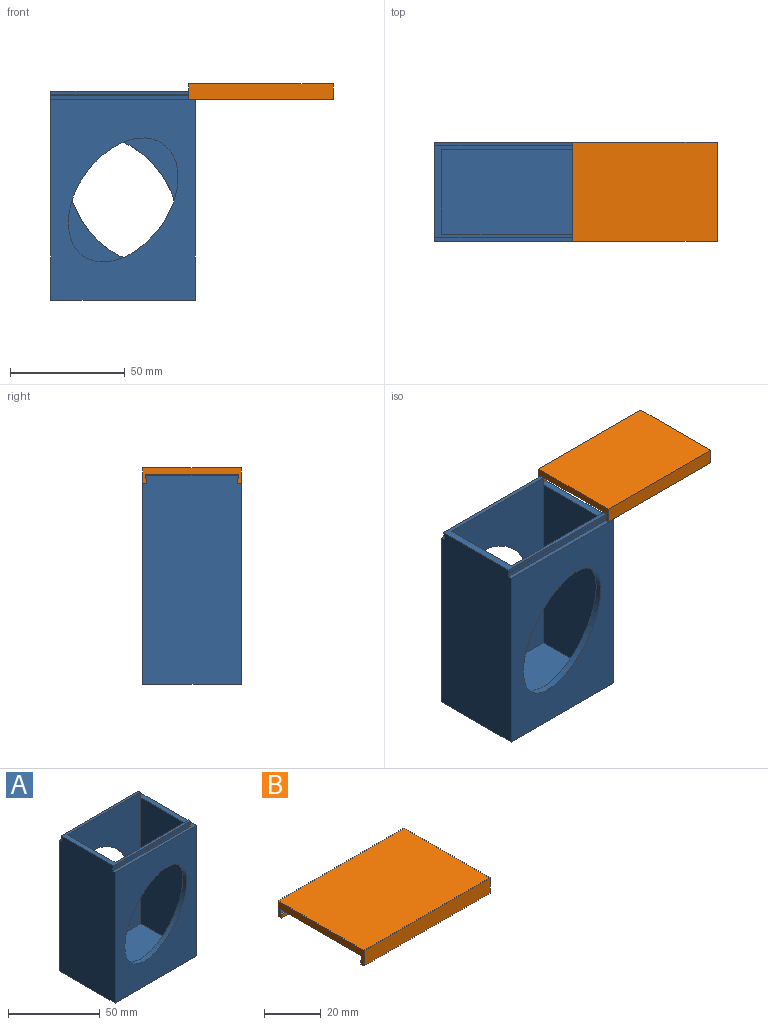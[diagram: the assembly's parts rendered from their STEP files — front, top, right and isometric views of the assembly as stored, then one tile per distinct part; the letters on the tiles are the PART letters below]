
ASSEMBLY  parts=2 mates=1
PART A: 22 faces, bbox 63x43x91 mm
  f0: plane 3.68x1.6mm, normal (1,0,0), area 5.1mm2, adj f4,f5,f6,f7,f8,f12
  f1: plane 3.68x1.6mm, normal (1,0,0), area 5.1mm2, adj f2,f5,f12,f13,f14,f15
  f2: plane 88x57mm, normal (0,-1,0), area 3131mm2, adj f1,f3,f5,f17,f18,f21
  f3: plane 57x37mm, normal (0,0,1), area 2109mm2, adj f2,f4,f17,f18
  f4: plane 88x57mm, normal (0,1,0), area 3131mm2, adj f0,f3,f5,f17,f18,f20
  f5: plane 60x40.2mm, normal (0,0,1), area 303mm2, adj f0,f1,f2,f4,f6,f15,f16,f17
  f6: plane 60x1.5mm, normal (0,-1,0), area 90mm2, adj f0,f5,f7,f16
  f7: plane 60x0.4mm, normal (0,-0.71,-0.71), area 33.9mm2, adj f0,f6,f8,f16
  f8: plane 60x1.78mm, normal (0,-1,0), area 107mm2, adj f0,f7,f12,f16
  f9: plane 87.32x63mm, normal (0,-1,0), area 3616mm2, adj f10,f12,f16,f19,f20
  f10: plane 63x43mm, normal (0,0,-1), area 2709mm2, adj f9,f11,f16,f19
  f11: plane 87.32x63mm, normal (0,1,0), area 3616mm2, adj f10,f12,f16,f19,f21
  f12: plane 63x43mm, normal (0,0,1), area 345mm2, adj f0,f1,f8,f9,f11,f13,f16,f18
  f13: plane 60x1.78mm, normal (0,1,0), area 107mm2, adj f1,f12,f14,f16
  f14: plane 60x0.4mm, normal (0,0.71,-0.71), area 33.9mm2, adj f1,f13,f15,f16
  f15: plane 60x1.5mm, normal (0,1,0), area 90mm2, adj f1,f5,f14,f16
  f16: plane 91x43mm, normal (-1,0,0), area 3901.1mm2, adj f5,f6,f7,f8,f9,f10,f11,f12
  f17: plane 88x37mm, normal (1,0,0), area 3256mm2, adj f2,f3,f4,f5
  f18: plane 84.32x37mm, normal (-1,0,0), area 3119.7mm2, adj f2,f3,f4,f12
  f19: plane 87.32x43mm, normal (1,0,0), area 3754.6mm2, adj f9,f10,f11,f12
  f20: extruded ~53.91x47.76mm, area 476mm2, adj f4,f9
  f21: extruded ~53.91x47.76mm, area 476mm2, adj f2,f11
PART B: 14 faces, bbox 63x43x6.7 mm
  f0: plane 60x1.5mm, normal (0,1,0), area 90mm2, adj f1,f10,f11,f13
  f1: plane 60x0.4mm, normal (0,0.71,0.71), area 33.9mm2, adj f0,f2,f11,f13
  f2: plane 60x1.78mm, normal (0,1,0), area 107mm2, adj f1,f3,f11,f13
  f3: plane 60x40.6mm, normal (0,0,-1), area 2436mm2, adj f2,f4,f11,f13
  f4: plane 60x1.78mm, normal (0,-1,0), area 107mm2, adj f3,f5,f11,f13
  f5: plane 60x0.4mm, normal (0,-0.71,0.71), area 33.9mm2, adj f4,f6,f11,f13
  f6: plane 60x1.5mm, normal (0,-1,0), area 90mm2, adj f5,f10,f11,f13
  f7: plane 63x6.68mm, normal (0,1,0), area 421mm2, adj f8,f10,f11,f12
  f8: plane 63x43mm, normal (0,0,1), area 2709mm2, adj f7,f9,f11,f12
  f9: plane 63x6.68mm, normal (0,-1,0), area 421mm2, adj f8,f10,f11,f12
  f10: plane 63x43mm, normal (0,0,-1), area 321mm2, adj f0,f6,f7,f9,f11,f12,f13
  f11: plane 43x6.68mm, normal (-1,0,0), area 139.2mm2, adj f0,f1,f2,f3,f4,f5,f6,f7
  f12: plane 43x6.68mm, normal (1,0,0), area 287.4mm2, adj f7,f8,f9,f10
  f13: plane 40.6x3.68mm, normal (-1,0,0), area 148.2mm2, adj f0,f1,f2,f3,f4,f5,f6,f10
PLACE A t=(-13.42,-2.76,-0.07)mm fixed
PLACE B t=(46.58,-2.76,-0.07)mm
MATE slider A.f16 <-> B.f11  axis (-1,0,0) through (-16.42,-24.26,40.25)mm
